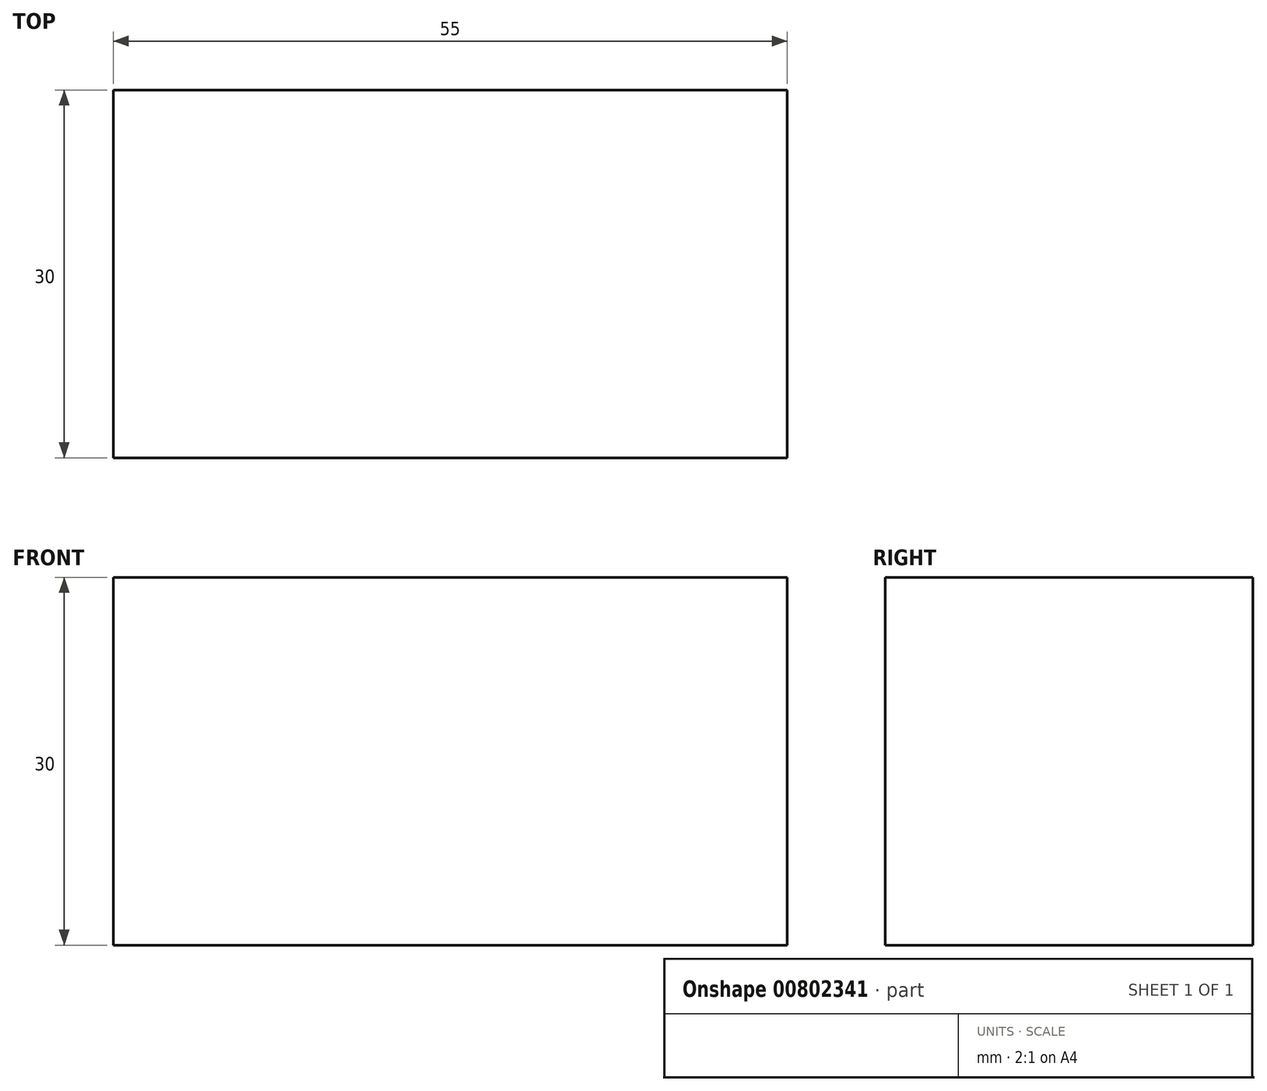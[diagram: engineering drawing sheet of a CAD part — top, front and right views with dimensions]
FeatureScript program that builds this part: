
annotation { "Feature Type Name" : "Feature", "Feature Type Description" : "" }
export const myFeature = defineFeature(function(context is Context, id is Id, definition is map)
    precondition{}
    {
        {
            var Q0;
            Q0=qCreatedBy(makeId("Top.planeOp"),FACE);
            var sketch = newSketch(context, id + "F0", { "sketchPlane" : qUnion([Q0])});
            skLineSegment(sketch, "E0.bottom", {"start": v(-10.36, -2.79) * mm, "end": v(-65.36, -2.79) * mm});
            skLineSegment(sketch, "E0.top", {"start": v(-10.36, -32.79) * mm, "end": v(-65.36, -32.79) * mm});
            skLineSegment(sketch, "E0.left", {"start": v(-10.36, -2.79) * mm, "end": v(-10.36, -32.79) * mm});
            skLineSegment(sketch, "E0.right", {"start": v(-65.36, -2.79) * mm, "end": v(-65.36, -32.79) * mm});
            skPoint(sketch, "E0.middle", {"position": v(-37.86, -17.79) * mm});
            skSolve(sketch);
        }
        {
            var Q0;
            Q0=makeQuery(id+"F0.imprint","IMPRINT",FACE,{"disambiguationData":[TD([[makeQuery(id+"F0.imprint","IMPRINT",EDGE,{"derivedFrom":sQuery(id+"F0.wireOp",EDGE,"E0.bottom")}),1.0]])]});
            extrude(context, id + "F1", {"entities" : qUnion([Q0]), "depth" : 30 * mm, "offsetDistance" : 25 * mm});
        }
    });
